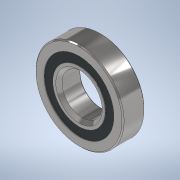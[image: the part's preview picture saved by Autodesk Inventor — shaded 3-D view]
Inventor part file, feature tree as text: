
AUTODESK INVENTOR PART (.ipt)
format: ipt  version: 2020 (Build 240168000, 168)  size: 609,792 bytes
history: native  units: in
note: dims shown in document units (in); Inventor stores cm internally (conversion verified against a paired STEP export)
features: other x11, revolve x5
ambient origin geometry x8: Origin, YZ Plane, XZ Plane, XY Plane, X Axis, Y Axis, Z Axis, Center Point
bodies: Solid1 (feature_tree), Solid2 (feature_tree), Solid3 (feature_tree), Solid4 (feature_tree), Solid5 (feature_tree), Solid6 (feature_tree), Solid7 (feature_tree), Solid8 (feature_tree), Solid9 (feature_tree), Solid10 (feature_tree), Solid11 (feature_tree), Solid12 (feature_tree), Solid13 (feature_tree), Solid14 (feature_tree), Solid15 (feature_tree), Solid16 (feature_tree)
feature tree (16):
  revolve  "Revolve1"  [1 undecoded]
  revolve  "Revolve3"  [1 undecoded]
  revolve  "Revolve4"  [1 undecoded]
  other  "CirPattern1[1]"
  other  "CirPattern1[2]"
  other  "CirPattern1[3]"
  other  "CirPattern1[4]"
  other  "CirPattern1[5]"
  other  "CirPattern1[6]"
  other  "CirPattern1[7]"
  other  "CirPattern1[8]"
  other  "CirPattern1[9]"
  other  "CirPattern1[10]"
  other  "CirPattern1[11]"
  revolve  "Revolve5[1]"  [1 undecoded]
  revolve  "Revolve5[2]"  [1 undecoded]
note: 5 required parameter values undecoded (feature->parameter linkage not recoverable at this tier; creation-order binding heuristic only, values carry confidence <= 0.55)
